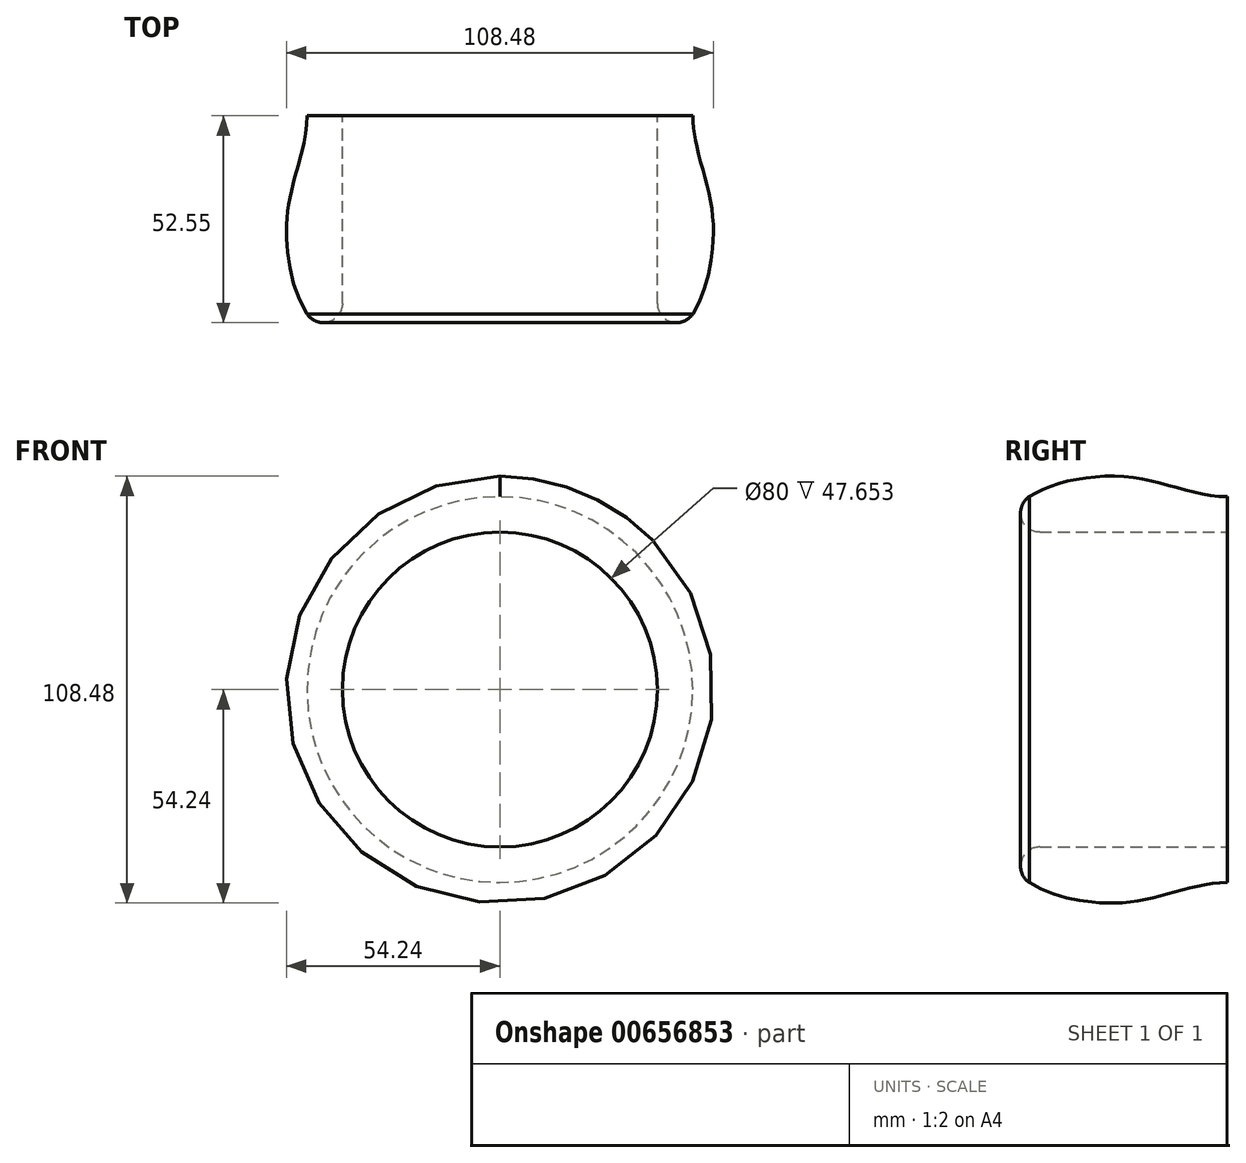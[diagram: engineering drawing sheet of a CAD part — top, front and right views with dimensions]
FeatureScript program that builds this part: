
annotation { "Feature Type Name" : "Feature", "Feature Type Description" : "" }
export const myFeature = defineFeature(function(context is Context, id is Id, definition is map)
    precondition{}
    {
        {
            var Q0;
            Q0=qCreatedBy(makeId("Right.planeOp"),FACE);
            var sketch = newSketch(context, id + "F0", { "sketchPlane" : qUnion([Q0])});
            skLineSegment(sketch, "E0.top", {"start": v(-47.65, 40) * mm, "end": v(0, 40) * mm});
            skFitSpline(sketch, "E1", {"points": [v(-50.34, 49) * mm, v(-25, 54) * mm, v(0, 49) * mm, v(25, 54) * mm, v(50, 50) * mm], "startDerivative": vector(70.76, 46.4) * mm, "endDerivative": vector(118.22, -38.67) * mm});
            skArc(sketch, "E2", {"start": v(-50.34, 49) * mm, "mid": v(-52.35, 43.5) * mm, "end": v(-47.65, 40) * mm});
            skLineSegment(sketch, "E3", {"start": v(0, 49) * mm, "end": v(0, 40) * mm});
            skSolve(sketch);
        }
        {
            var Q0;
            Q0=qCreatedBy(makeId("Top.planeOp"),FACE);
            var sketch = newSketch(context, id + "F1", { "sketchPlane" : qUnion([Q0])});
            skLineSegment(sketch, "E4", {"start": v(0, 0) * mm, "end": v(0, -67.6) * mm});
            skSolve(sketch);
        }
        {
            var Q0;
            Q0 = qSketchRegion(id + "F0", true);
            var Q1;
            Q1=sQuery(id+"F1.wireOp",EDGE,"E4");
            revolve(context, id + "F2", {"entities" : qUnion([Q0]), "axis" : qUnion([Q1]), "revolveType" : RevolveType.FULL});
        }
    });
